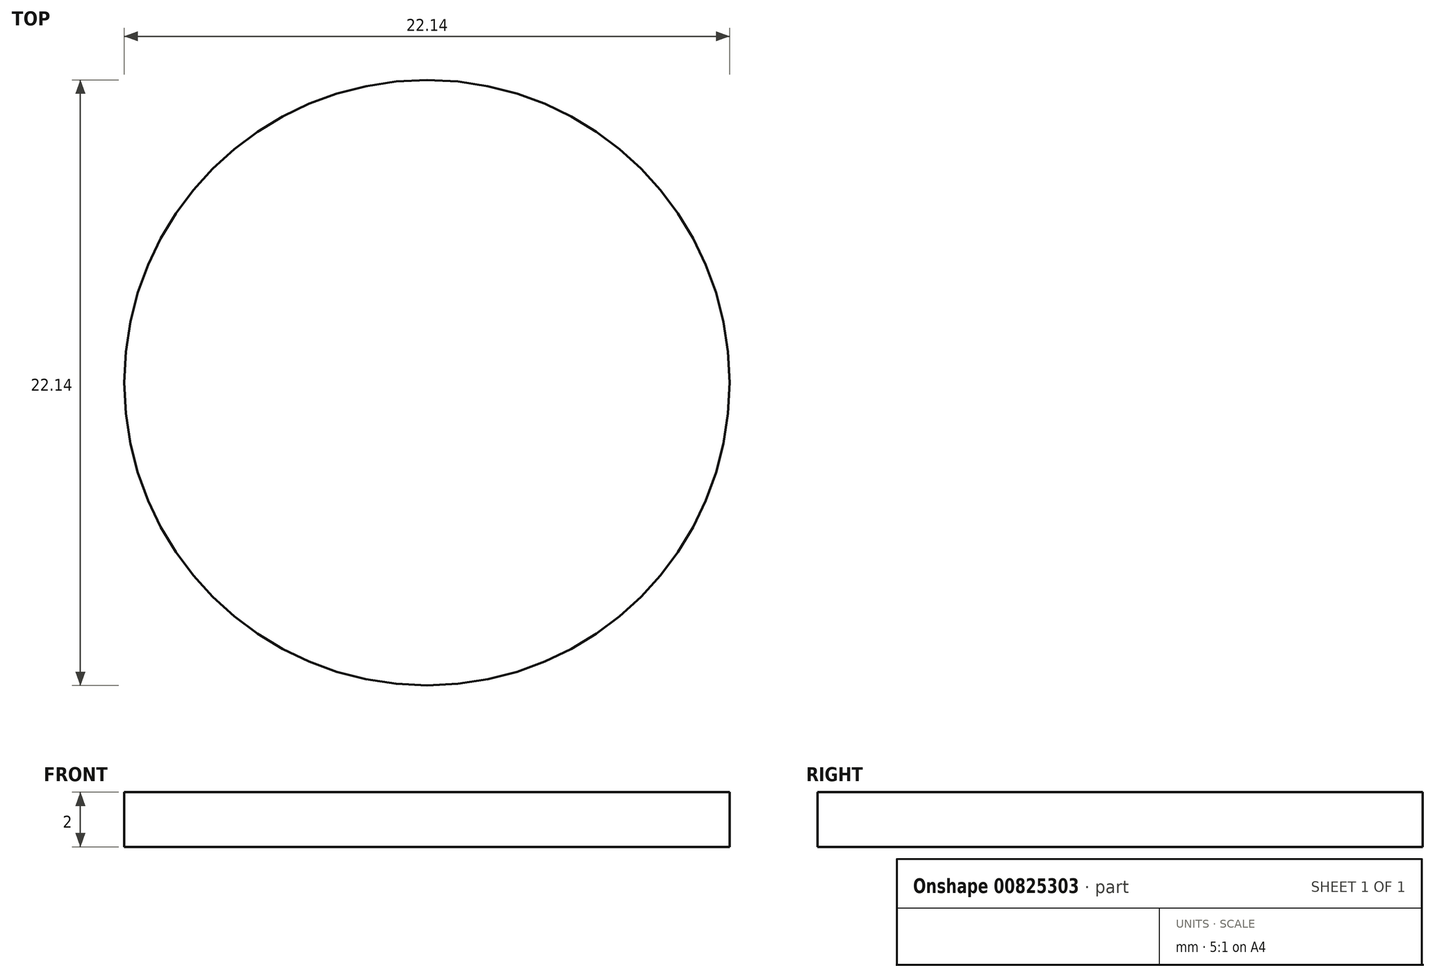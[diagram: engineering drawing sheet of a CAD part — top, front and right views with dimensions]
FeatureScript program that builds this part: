
annotation { "Feature Type Name" : "Feature", "Feature Type Description" : "" }
export const myFeature = defineFeature(function(context is Context, id is Id, definition is map)
    precondition{}
    {
        {
            var Q0;
            Q0=qCreatedBy(makeId("Top.planeOp"),FACE);
            var sketch = newSketch(context, id + "F0", { "sketchPlane" : qUnion([Q0])});
            skCircle(sketch, "E0", {"center": v(0, 0) * mm, "radius": 11.07 * mm});
            skSolve(sketch);
        }
        {
            var Q0;
            Q0=makeQuery(id+"F0.imprint","IMPRINT",FACE,{"disambiguationData":[TD([[makeQuery(id+"F0.imprint","IMPRINT",EDGE,{"derivedFrom":sQuery(id+"F0.wireOp",EDGE,"E0")}),1.0]])]});
            extrude(context, id + "F1", {"entities" : qUnion([Q0]), "depth" : 2 * mm, "offsetDistance" : 25 * mm});
        }
    });
